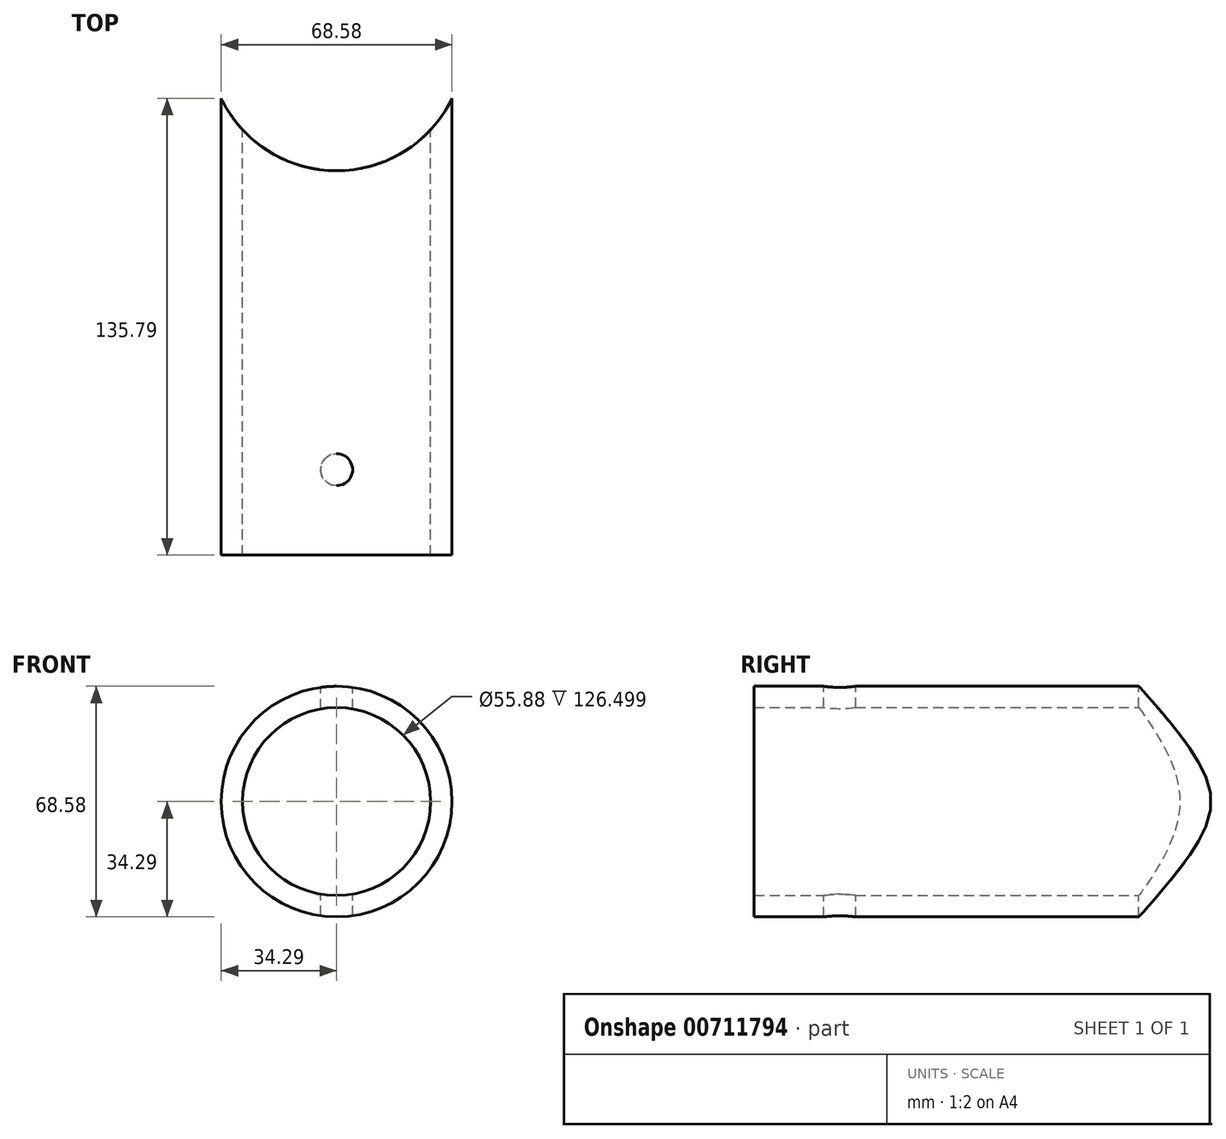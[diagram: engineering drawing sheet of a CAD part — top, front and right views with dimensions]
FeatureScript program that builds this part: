
annotation { "Feature Type Name" : "Feature", "Feature Type Description" : "" }
export const myFeature = defineFeature(function(context is Context, id is Id, definition is map)
    precondition{}
    {
        {
            var Q0;
            Q0=qCreatedBy(makeId("Front.planeOp"),FACE);
            var sketch = newSketch(context, id + "F0", { "sketchPlane" : qUnion([Q0])});
            skCircle(sketch, "E0", {"center": v(0, 0) * mm, "radius": 34.3 * mm});
            skCircle(sketch, "E1", {"center": v(0, 0) * mm, "radius": 27.94 * mm});
            skSolve(sketch);
        }
        {
            var Q0;
            Q0 = qSketchRegion(id + "F0", true);
            extrude(context, id + "F1", {"entities" : qUnion([Q0]), "endBound" : BoundingType.SYMMETRIC, "depth" : 152.4 * mm, "offsetDistance" : 25.4 * mm});
        }
        {
            var Q0;
            Q0=qCreatedBy(makeId("Top.planeOp"),FACE);
            var sketch = newSketch(context, id + "F2", { "sketchPlane" : qUnion([Q0])});
            skCircle(sketch, "E2", {"center": v(0, -50.8) * mm, "radius": 4.76 * mm});
            skSolve(sketch);
        }
        {
            var Q0;
            Q0 = qSketchRegion(id + "F2", true);
            extrude(context, id + "F3", {"entities" : qUnion([Q0]), "operationType" : NewBodyOperationType.REMOVE, "endBound" : BoundingType.SYMMETRIC, "oppositeDirection" : true, "depth" : 76.2 * mm, "offsetDistance" : 25.4 * mm});
        }
        {
            var Q0;
            Q0=qCreatedBy(makeId("Top.planeOp"),FACE);
            var sketch = newSketch(context, id + "F4", { "sketchPlane" : qUnion([Q0])});
            skCircle(sketch, "E3", {"center": v(0, 76.2) * mm, "radius": 38.1 * mm});
            skSolve(sketch);
        }
        {
            var Q0;
            Q0 = qSketchRegion(id + "F4", true);
            extrude(context, id + "F5", {"entities" : qUnion([Q0]), "operationType" : NewBodyOperationType.REMOVE, "endBound" : BoundingType.SYMMETRIC, "oppositeDirection" : true, "depth" : 76.2 * mm, "offsetDistance" : 25.4 * mm});
        }
    });
